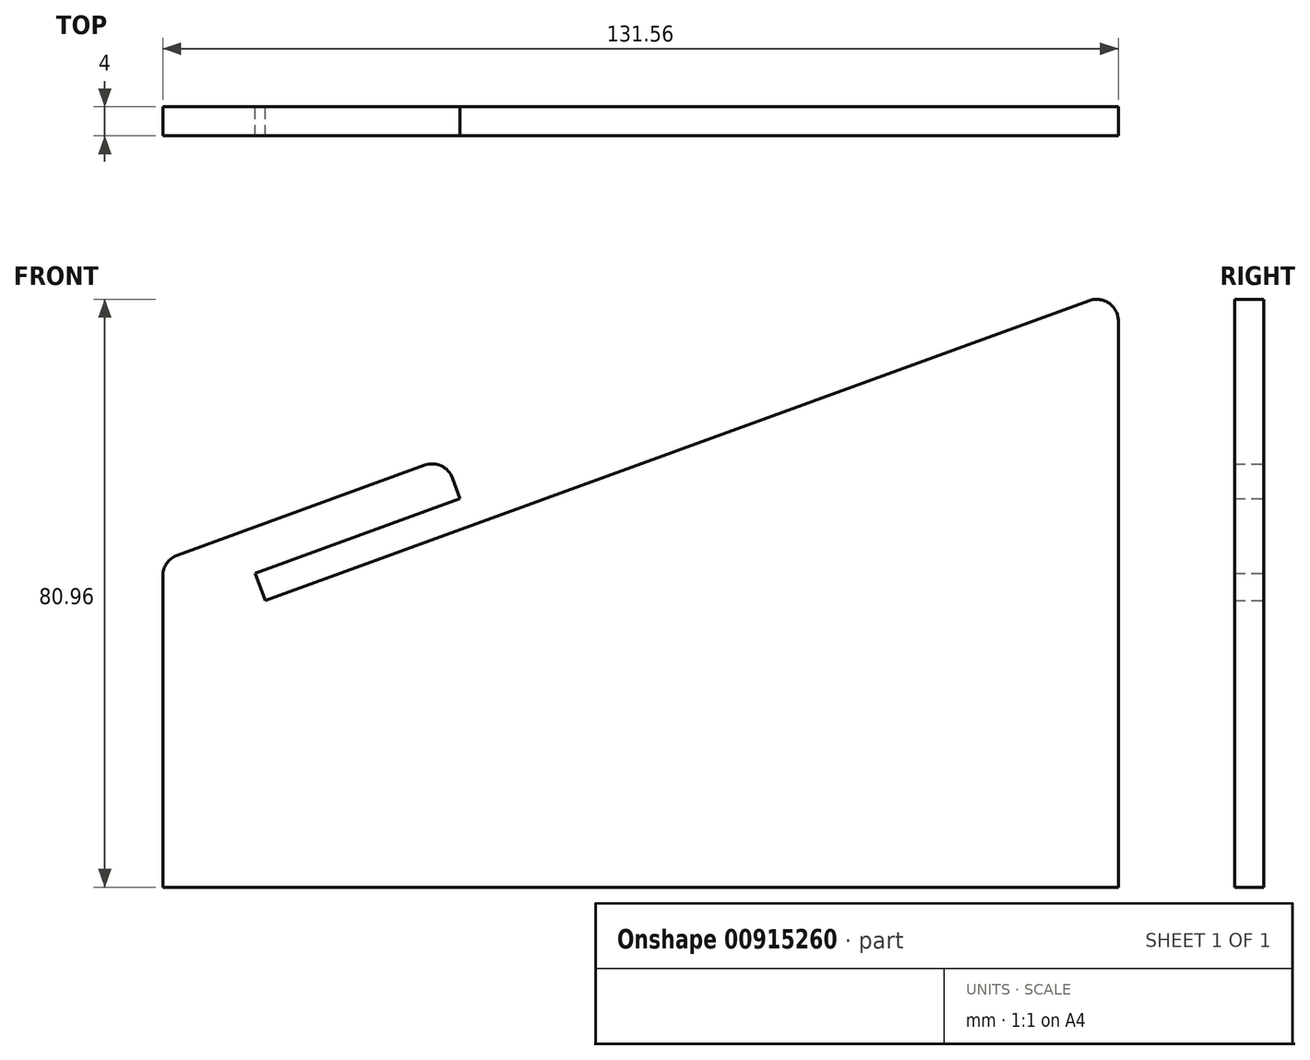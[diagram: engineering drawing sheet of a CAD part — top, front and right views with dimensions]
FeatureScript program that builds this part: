
annotation { "Feature Type Name" : "Feature", "Feature Type Description" : "" }
export const myFeature = defineFeature(function(context is Context, id is Id, definition is map)
    precondition{}
    {
        {
            var Q0;
            Q0=qCreatedBy(makeId("Front.planeOp"),FACE);
            var sketch = newSketch(context, id + "F0", { "sketchPlane" : qUnion([Q0])});
            skLineSegment(sketch, "E0", {"start": v(-131.56, 0) * mm, "end": v(0, 0) * mm});
            skLineSegment(sketch, "E1", {"start": v(0, 0) * mm, "end": v(0, 82.24) * mm});
            skLineSegment(sketch, "E2", {"start": v(0, 82.24) * mm, "end": v(-117.46, 39.49) * mm});
            skLineSegment(sketch, "E3", {"start": v(-117.46, 39.49) * mm, "end": v(-118.83, 43.25) * mm});
            skLineSegment(sketch, "E4", {"start": v(-118.83, 43.25) * mm, "end": v(-90.64, 53.5) * mm});
            skLineSegment(sketch, "E5", {"start": v(-90.64, 53.5) * mm, "end": v(-92.7, 59.15) * mm});
            skLineSegment(sketch, "E6", {"start": v(-92.7, 59.15) * mm, "end": v(-131.56, 45) * mm});
            skLineSegment(sketch, "E7", {"start": v(-131.56, 45) * mm, "end": v(-131.56, 0) * mm});
            skLineSegment(sketch, "E8", {"start": v(-117.46, 39.49) * mm, "end": v(-131.56, 34.36) * mm, "construction": true});
            skSolve(sketch);
        }
        {
            var Q0;
            Q0 = qSketchRegion(id + "F0", true);
            extrude(context, id + "F1", {"entities" : qUnion([Q0]), "depth" : 4 * mm, "offsetDistance" : 25 * mm});
        }
        {
            var Q0;
            Q0=makeQuery(id+"F1.opExtrude","SWEPT_EDGE",EDGE,{"disambiguationData":[OSD([sQuery(id+"F0.wireOp",EDGE,"E6"),sQuery(id+"F0.wireOp",EDGE,"E7")])]});
            var Q1;
            Q1=makeQuery(id+"F1.opExtrude","SWEPT_EDGE",EDGE,{"disambiguationData":[OSD([sQuery(id+"F0.wireOp",EDGE,"E1"),sQuery(id+"F0.wireOp",EDGE,"E2")])]});
            var Q2;
            Q2=makeQuery(id+"F1.opExtrude","SWEPT_EDGE",EDGE,{"disambiguationData":[OSD([sQuery(id+"F0.wireOp",EDGE,"E5"),sQuery(id+"F0.wireOp",EDGE,"E6")])]});
            fillet(context, id + "F2", {"entities" : qUnion([Q0, Q1, Q2]), "radius" : 3 * mm, "tangentPropagation" : true, "allowEdgeOverflow" : false});
        }
    });
